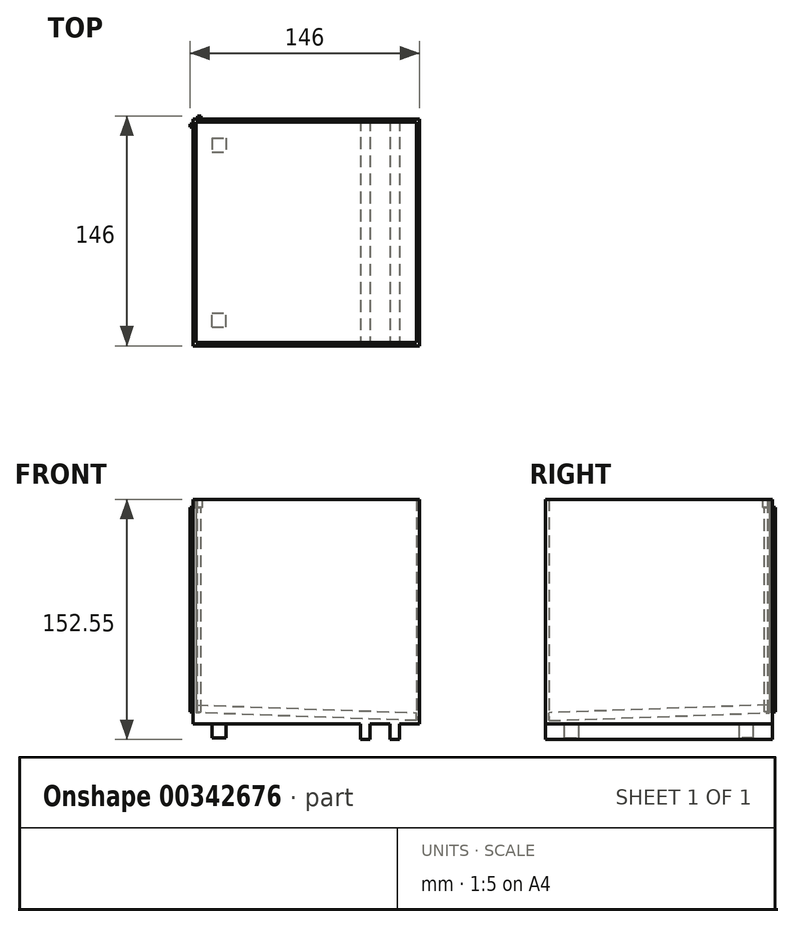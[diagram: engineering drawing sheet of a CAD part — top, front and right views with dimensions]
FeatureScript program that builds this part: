
annotation { "Feature Type Name" : "Feature", "Feature Type Description" : "" }
export const myFeature = defineFeature(function(context is Context, id is Id, definition is map)
    precondition{}
    {
        {
            var Q0;
            Q0=qCreatedBy(makeId("Top.planeOp"),FACE);
            var sketch = newSketch(context, id + "F0", { "sketchPlane" : qUnion([Q0])});
            skLineSegment(sketch, "E0.bottom", {"start": v(0, 0) * mm, "end": v(-144, 0) * mm});
            skLineSegment(sketch, "E0.top", {"start": v(0, 144) * mm, "end": v(-144, 144) * mm});
            skLineSegment(sketch, "E0.left", {"start": v(0, 0) * mm, "end": v(0, 144) * mm});
            skLineSegment(sketch, "E0.right", {"start": v(-144, 0) * mm, "end": v(-144, 144) * mm});
            skSolve(sketch);
        }
        {
            var Q0;
            Q0 = qSketchRegion(id + "F0", true);
            extrude(context, id + "F1", {"entities" : qUnion([Q0]), "depth" : 25 * mm});
        }
        {
            var Q0;
            Q0 = qSketchRegion(id + "F0", true);
            extrude(context, id + "F2", {"entities" : qUnion([Q0]), "operationType" : NewBodyOperationType.ADD, "depth" : 142.55 * mm});
        }
        {
            var Q0;
            Q0=makeQuery(id+"F2.opExtrude","CAP_FACE",FACE,{"disambiguationData":[OSD([sQuery(id+"F0.wireOp",EDGE,"E0.bottom"),sQuery(id+"F0.wireOp",EDGE,"E0.top"),sQuery(id+"F0.wireOp",EDGE,"E0.left"),sQuery(id+"F0.wireOp",EDGE,"E0.right")])],"isStart":false});
            shell(context, id + "F3", {"entities" : qUnion([Q0]), "thickness" : 2 * mm});
        }
        {
            var Q0;
            Q0=makeQuery(id+"F3.opShell","OFFSET_FACE",FACE,{"disambiguationData":[OSD([sQuery(id+"F0.wireOp",EDGE,"E0.right")])]});
            var sketch = newSketch(context, id + "F4", { "sketchPlane" : qUnion([Q0])});
            skLineSegment(sketch, "E1", {"start": v(142, 2) * mm, "end": v(142, 12) * mm});
            skLineSegment(sketch, "E2", {"start": v(2, 2) * mm, "end": v(2, 7) * mm});
            skLineSegment(sketch, "E3.0.0", {"start": v(2, 2) * mm, "end": v(142, 2) * mm});
            skLineSegment(sketch, "E3.0.2", {"start": v(142, 2) * mm, "end": v(2, 2) * mm});
            skSolve(sketch);
        }
        {
            var Q0;
            Q0=makeQuery(id+"F3.opShell","OFFSET_FACE",FACE,{"disambiguationData":[OSD([sQuery(id+"F0.wireOp",EDGE,"E0.bottom"),sQuery(id+"F0.wireOp",EDGE,"E0.top"),sQuery(id+"F0.wireOp",EDGE,"E0.left"),sQuery(id+"F0.wireOp",EDGE,"E0.right")])]});
            var sketch = newSketch(context, id + "F5", { "sketchPlane" : qUnion([Q0])});
            skPoint(sketch, "E4", {"position": v(-2, 2) * mm});
            skSolve(sketch);
        }
        {
            var Q0;
            Q0=sQuery(id+"F5.wireOp",VERTEX,"E4");
            var Q1;
            Q1=sQuery(id+"F4.wireOp",VERTEX,"E1.end");
            var Q2;
            Q2=sQuery(id+"F4.wireOp",VERTEX,"E2.end");
            cPlane(context, id + "F6", {"entities" : qUnion([Q0, Q1, Q2]), "cplaneType" : CPlaneType.THREE_POINT, "offset" : 25 * mm, "width" : 150 * mm, "height" : 150 * mm});
        }
        {
            var Q0;
            Q0=makeQuery(id+"F3.opShell","OFFSET_FACE",FACE,{"disambiguationData":[OSD([sQuery(id+"F0.wireOp",EDGE,"E0.left")])]});
            var sketch = newSketch(context, id + "F7", { "sketchPlane" : qUnion([Q0])});
            skLineSegment(sketch, "E5", {"start": v(-142, 2) * mm, "end": v(-142, 7) * mm});
            skSolve(sketch);
        }
        {
            var Q0;
            Q0=qCreatedBy(id+"F6.planeOp",FACE);
            var sketch = newSketch(context, id + "F8", { "sketchPlane" : qUnion([Q0])});
            skPoint(sketch, "E6.0", {"position": v(-2.07, -142.16) * mm});
            skPoint(sketch, "E7.0", {"position": v(-142.16, -142.34) * mm});
            skPoint(sketch, "E8.0", {"position": v(-142.16, -2.25) * mm});
            skPoint(sketch, "E9.0", {"position": v(-2.07, -2.07) * mm});
            skLineSegment(sketch, "E10", {"start": v(-2.07, -2.07) * mm, "end": v(-2.07, -142.16) * mm});
            skLineSegment(sketch, "E11", {"start": v(-142.16, -142.34) * mm, "end": v(-2.07, -142.16) * mm});
            skLineSegment(sketch, "E12", {"start": v(-142.16, -142.34) * mm, "end": v(-142.16, -2.25) * mm});
            skLineSegment(sketch, "E13", {"start": v(-2.07, -2.07) * mm, "end": v(-142.16, -2.25) * mm});
            skSolve(sketch);
        }
        {
            var Q1;
            Q1=makeQuery(id+"F1.opExtrude","CAP_FACE",FACE,{"disambiguationData":[OSD([sQuery(id+"F0.wireOp",EDGE,"E0.bottom"),sQuery(id+"F0.wireOp",EDGE,"E0.top"),sQuery(id+"F0.wireOp",EDGE,"E0.left"),sQuery(id+"F0.wireOp",EDGE,"E0.right")])],"isStart":true});
            var Q2;
            Q2 = qSketchRegion(id + "F8", true);
            loft(context, id + "F9", {"operationType" : NewBodyOperationType.ADD, "sheetProfilesArray" : [{ "sheetProfileEntities" : qUnion([Q1]) }, { "sheetProfileEntities" : qUnion([Q2]) }]});
        }
        {
            var Q0;
            Q0=makeQuery(id+"F2.opExtrude","CAP_FACE",FACE,{"disambiguationData":[OSD([sQuery(id+"F0.wireOp",EDGE,"E0.bottom"),sQuery(id+"F0.wireOp",EDGE,"E0.top"),sQuery(id+"F0.wireOp",EDGE,"E0.left"),sQuery(id+"F0.wireOp",EDGE,"E0.right")])],"isStart":false});
            var sketch = newSketch(context, id + "F10", { "sketchPlane" : qUnion([Q0])});
            skLineSegment(sketch, "E14", {"start": v(-138, 142) * mm, "end": v(-141, 144) * mm});
            skLineSegment(sketch, "E15", {"start": v(-141, 144) * mm, "end": v(-144, 144) * mm});
            skLineSegment(sketch, "E16", {"start": v(-144, 144) * mm, "end": v(-144, 141) * mm});
            skLineSegment(sketch, "E17", {"start": v(-144, 141) * mm, "end": v(-142, 138) * mm});
            skLineSegment(sketch, "E18", {"start": v(-142, 138) * mm, "end": v(-142, 142) * mm});
            skLineSegment(sketch, "E19", {"start": v(-142, 142) * mm, "end": v(-138, 142) * mm});
            skSolve(sketch);
        }
        {
            var Q0;
            Q0 = qSketchRegion(id + "F10", true);
            extrude(context, id + "F11", {"entities" : qUnion([Q0]), "operationType" : NewBodyOperationType.REMOVE, "oppositeDirection" : true, "depth" : 5 * mm});
        }
        {
            var Q0;
            Q0=makeQuery(id+"F11.boolean.opBoolean","COPY",FACE,{"derivedFrom":makeQuery(id+"F11.opExtrude","CAP_FACE",FACE,{"disambiguationData":[OSD([sQuery(id+"F10.wireOp",EDGE,"E14"),sQuery(id+"F10.wireOp",EDGE,"E15"),sQuery(id+"F10.wireOp",EDGE,"E16"),sQuery(id+"F10.wireOp",EDGE,"E17"),sQuery(id+"F10.wireOp",EDGE,"E18"),sQuery(id+"F10.wireOp",EDGE,"E19")])],"isStart":false})});
            var sketch = newSketch(context, id + "F12", { "sketchPlane" : qUnion([Q0])});
            skLineSegment(sketch, "E20.bottom", {"start": v(-141, 144) * mm, "end": v(-139, 144) * mm});
            skLineSegment(sketch, "E20.top", {"start": v(-141, 146) * mm, "end": v(-139, 146) * mm});
            skLineSegment(sketch, "E20.left", {"start": v(-141, 144) * mm, "end": v(-141, 146) * mm});
            skLineSegment(sketch, "E20.right", {"start": v(-139, 144) * mm, "end": v(-139, 146) * mm});
            skLineSegment(sketch, "E21.bottom", {"start": v(-144, 141) * mm, "end": v(-146, 141) * mm});
            skLineSegment(sketch, "E21.top", {"start": v(-144, 139) * mm, "end": v(-146, 139) * mm});
            skLineSegment(sketch, "E21.left", {"start": v(-144, 141) * mm, "end": v(-144, 139) * mm});
            skLineSegment(sketch, "E21.right", {"start": v(-146, 141) * mm, "end": v(-146, 139) * mm});
            skSolve(sketch);
        }
        {
            var Q0;
            Q0 = qSketchRegion(id + "F12", true);
            extrude(context, id + "F13", {"entities" : qUnion([Q0]), "operationType" : NewBodyOperationType.ADD, "oppositeDirection" : true, "depth" : 130 * mm});
        }
        {
            var Q0;
            Q0=makeQuery(id+"F1.opExtrude","CAP_FACE",FACE,{"disambiguationData":[OSD([sQuery(id+"F0.wireOp",EDGE,"E0.bottom"),sQuery(id+"F0.wireOp",EDGE,"E0.top"),sQuery(id+"F0.wireOp",EDGE,"E0.left"),sQuery(id+"F0.wireOp",EDGE,"E0.right")])],"isStart":true});
            var sketch = newSketch(context, id + "F14", { "sketchPlane" : qUnion([Q0])});
            skLineSegment(sketch, "E22.bottom", {"start": v(-13, -144) * mm, "end": v(-19, -144) * mm});
            skLineSegment(sketch, "E22.top", {"start": v(-13, 0) * mm, "end": v(-19, 0) * mm});
            skLineSegment(sketch, "E22.left", {"start": v(-13, -144) * mm, "end": v(-13, 0) * mm});
            skLineSegment(sketch, "E22.right", {"start": v(-19, -144) * mm, "end": v(-19, 0) * mm});
            skLineSegment(sketch, "E23.bottom", {"start": v(-31.5, -144) * mm, "end": v(-37.5, -144) * mm});
            skLineSegment(sketch, "E23.top", {"start": v(-31.5, 0) * mm, "end": v(-37.5, 0) * mm});
            skLineSegment(sketch, "E23.left", {"start": v(-31.5, -144) * mm, "end": v(-31.5, 0) * mm});
            skLineSegment(sketch, "E23.right", {"start": v(-37.5, -144) * mm, "end": v(-37.5, 0) * mm});
            skLineSegment(sketch, "E24", {"start": v(-19, -144) * mm, "end": v(-31.5, -144) * mm, "construction": true});
            skLineSegment(sketch, "E25.0.0", {"start": v(0, 0) * mm, "end": v(0, -144) * mm});
            skLineSegment(sketch, "E25.0.2", {"start": v(0, -144) * mm, "end": v(0, 0) * mm});
            skLineSegment(sketch, "E26", {"start": v(0, -144) * mm, "end": v(-13, -144) * mm, "construction": true});
            skSolve(sketch);
        }
        {
            var Q0;
            Q0 = qSketchRegion(id + "F14", true);
            extrude(context, id + "F15", {"entities" : qUnion([Q0]), "operationType" : NewBodyOperationType.ADD, "depth" : 10 * mm});
        }
        {
            var Q0;
            {var subQ0=sQuery(id+"F0.wireOp",EDGE,"E0.right");var subQ1=sQuery(id+"F0.wireOp",EDGE,"E0.top");var subQ2=sQuery(id+"F0.wireOp",EDGE,"E0.bottom");Q0=makeQuery(id+"F15.boolean.opBoolean","SPLIT",FACE,{"disambiguationData":[TD([makeQuery(id+"F1.opExtrude","SWEPT_FACE",FACE,{"disambiguationData":[OSD([subQ0])]})])],"derivedFrom":makeQuery(id+"F1.opExtrude","CAP_FACE",FACE,{"disambiguationData":[OSD([subQ2,subQ1,sQuery(id+"F0.wireOp",EDGE,"E0.left"),subQ0])],"isStart":true})});}
            var sketch = newSketch(context, id + "F16", { "sketchPlane" : qUnion([Q0])});
            skLineSegment(sketch, "E27.bottom", {"start": v(-132, -132) * mm, "end": v(-123, -132) * mm});
            skLineSegment(sketch, "E27.top", {"start": v(-132, -123) * mm, "end": v(-123, -123) * mm});
            skLineSegment(sketch, "E27.left", {"start": v(-132, -132) * mm, "end": v(-132, -123) * mm});
            skLineSegment(sketch, "E27.right", {"start": v(-123, -132) * mm, "end": v(-123, -123) * mm});
            skLineSegment(sketch, "E28.0", {"start": v(-142, -142) * mm, "end": v(-2, -142) * mm, "construction": true});
            skLineSegment(sketch, "E29.0", {"start": v(-142, -142) * mm, "end": v(-142, -2) * mm, "construction": true});
            skLineSegment(sketch, "E30.0", {"start": v(-2, -2) * mm, "end": v(-142, -2) * mm, "construction": true});
            skLineSegment(sketch, "E31.bottom", {"start": v(-132, -12) * mm, "end": v(-123, -12) * mm});
            skLineSegment(sketch, "E31.top", {"start": v(-132, -21) * mm, "end": v(-123, -21) * mm});
            skLineSegment(sketch, "E31.left", {"start": v(-132, -12) * mm, "end": v(-132, -21) * mm});
            skLineSegment(sketch, "E31.right", {"start": v(-123, -12) * mm, "end": v(-123, -21) * mm});
            skSolve(sketch);
        }
        {
            var Q0;
            Q0 = qSketchRegion(id + "F16", true);
            extrude(context, id + "F17", {"entities" : qUnion([Q0]), "operationType" : NewBodyOperationType.ADD, "depth" : 9 * mm});
        }
    });
